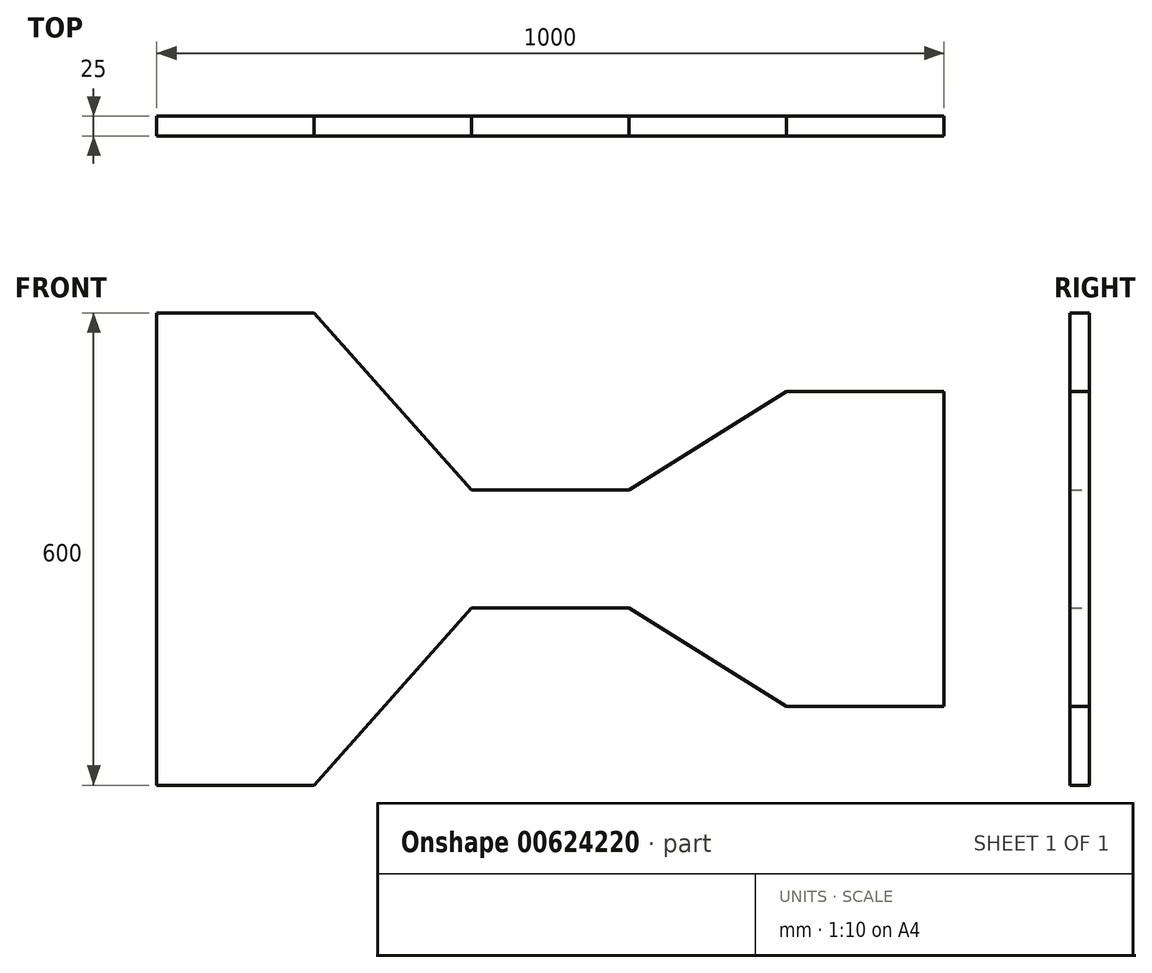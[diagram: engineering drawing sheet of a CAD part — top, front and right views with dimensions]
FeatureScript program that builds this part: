
annotation { "Feature Type Name" : "Feature", "Feature Type Description" : "" }
export const myFeature = defineFeature(function(context is Context, id is Id, definition is map)
    precondition{}
    {
        {
            var Q0;
            Q0=qCreatedBy(makeId("Front.planeOp"),FACE);
            var sketch = newSketch(context, id + "F0", { "sketchPlane" : qUnion([Q0])});
            skLineSegment(sketch, "E0", {"start": v(-500, 300) * mm, "end": v(-500, -300) * mm});
            skLineSegment(sketch, "E1", {"start": v(-500, 300) * mm, "end": v(-300, 300) * mm});
            skLineSegment(sketch, "E2", {"start": v(-500, -300) * mm, "end": v(-300, -300) * mm});
            skLineSegment(sketch, "E3", {"start": v(-100, 75) * mm, "end": v(100, 75) * mm});
            skLineSegment(sketch, "E4", {"start": v(-100, -75) * mm, "end": v(100, -75) * mm});
            skLineSegment(sketch, "E5", {"start": v(-300, 300) * mm, "end": v(-100, 75) * mm});
            skLineSegment(sketch, "E6", {"start": v(-300, -300) * mm, "end": v(-100, -75) * mm});
            skLineSegment(sketch, "E7", {"start": v(500, 200) * mm, "end": v(500, -200) * mm});
            skLineSegment(sketch, "E8", {"start": v(500, 200) * mm, "end": v(300, 200) * mm});
            skLineSegment(sketch, "E9", {"start": v(500, -200) * mm, "end": v(300, -200) * mm});
            skLineSegment(sketch, "E10", {"start": v(100, 75) * mm, "end": v(300, 200) * mm});
            skLineSegment(sketch, "E11", {"start": v(100, -75) * mm, "end": v(300, -200) * mm});
            skSolve(sketch);
        }
        {
            var Q0;
            Q0 = qSketchRegion(id + "F0", true);
            extrude(context, id + "F1", {"entities" : qUnion([Q0]), "depth" : 25 * mm, "offsetDistance" : 25 * mm});
        }
    });
